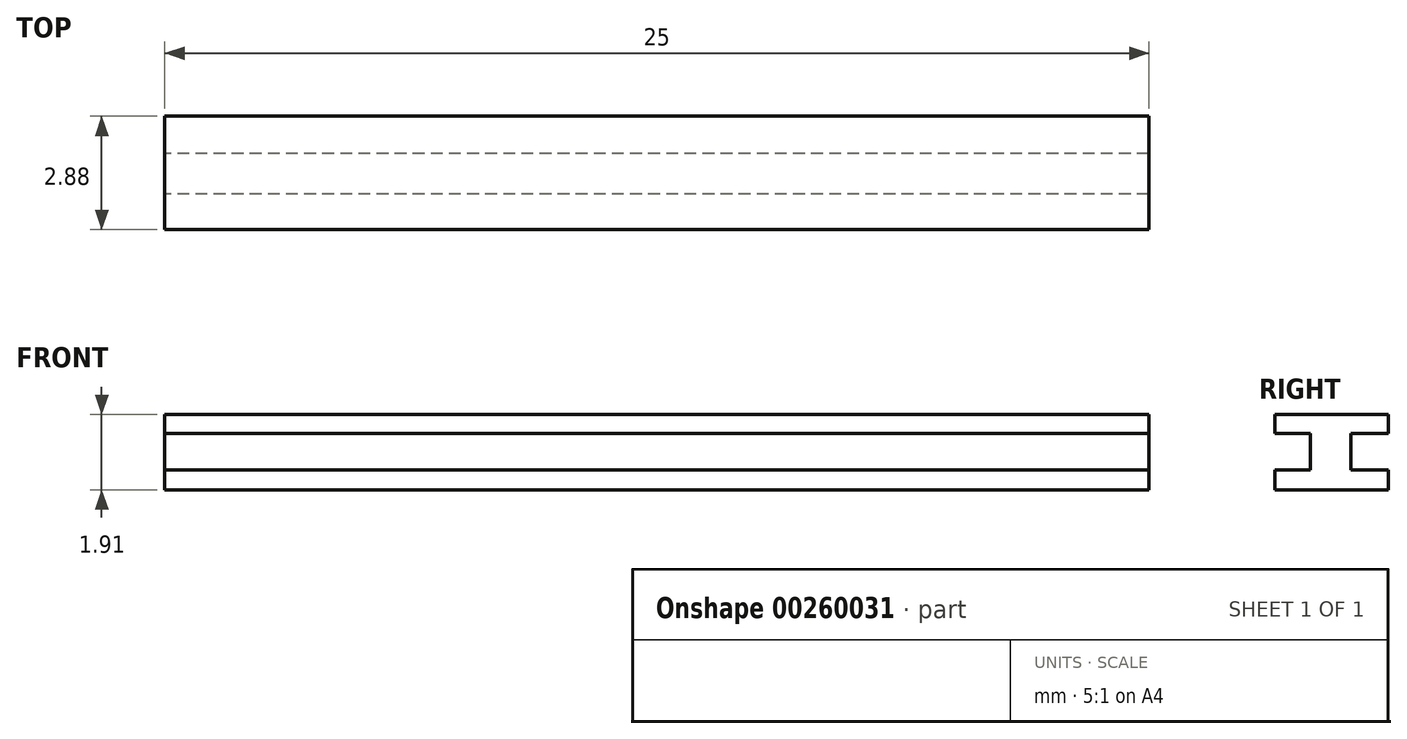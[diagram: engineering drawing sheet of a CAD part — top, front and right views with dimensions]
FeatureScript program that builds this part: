
annotation { "Feature Type Name" : "Feature", "Feature Type Description" : "" }
export const myFeature = defineFeature(function(context is Context, id is Id, definition is map)
    precondition{}
    {
        {
            var Q0;
            Q0=qCreatedBy(makeId("Right.planeOp"),FACE);
            var sketch = newSketch(context, id + "F0", { "sketchPlane" : qUnion([Q0])});
            skLineSegment(sketch, "E0.right", {"start": v(-2.88, 0) * mm, "end": v(-2.88, 0.5) * mm});
            skLineSegment(sketch, "E1.top", {"start": v(-2.88, 1.9) * mm, "end": v(0, 1.9) * mm});
            skLineSegment(sketch, "E2.top", {"start": v(-2.88, 0) * mm, "end": v(0, 0) * mm});
            skLineSegment(sketch, "E3.top", {"start": v(-2.88, 1.42) * mm, "end": v(-1.98, 1.42) * mm});
            skLineSegment(sketch, "E3.left", {"start": v(-2.88, 1.9) * mm, "end": v(-2.88, 1.42) * mm});
            skLineSegment(sketch, "E4.top", {"start": v(-2.88, 0.5) * mm, "end": v(-1.98, 0.5) * mm});
            skLineSegment(sketch, "E5.right", {"start": v(0, 1.9) * mm, "end": v(0, 1.42) * mm});
            skLineSegment(sketch, "E6.trimOffspring", {"start": v(-2.88, 0.5) * mm, "end": v(-2.88, 0) * mm});
            skLineSegment(sketch, "E7.trimOffspring", {"start": v(-2.88, 1.42) * mm, "end": v(-2.88, 1.9) * mm});
            skLineSegment(sketch, "E8.trimOffspring", {"start": v(0, 0.5) * mm, "end": v(0, 0) * mm});
            skLineSegment(sketch, "E9.trimOffspring", {"start": v(-0.95, 0.5) * mm, "end": v(0, 0.5) * mm});
            skLineSegment(sketch, "E10.trimOffspring", {"start": v(-0.95, 1.42) * mm, "end": v(0, 1.42) * mm});
            skLineSegment(sketch, "E11.trimOffspring", {"start": v(-1.98, 1.42) * mm, "end": v(-1.98, 0.5) * mm});
            skLineSegment(sketch, "E12.trimOffspring", {"start": v(-0.95, 1.42) * mm, "end": v(-0.95, 0.5) * mm});
            skSolve(sketch);
        }
        {
            var Q0;
            Q0 = qSketchRegion(id + "F0", true);
            extrude(context, id + "F1", {"entities" : qUnion([Q0]), "depth" : 25 * mm});
        }
    });
